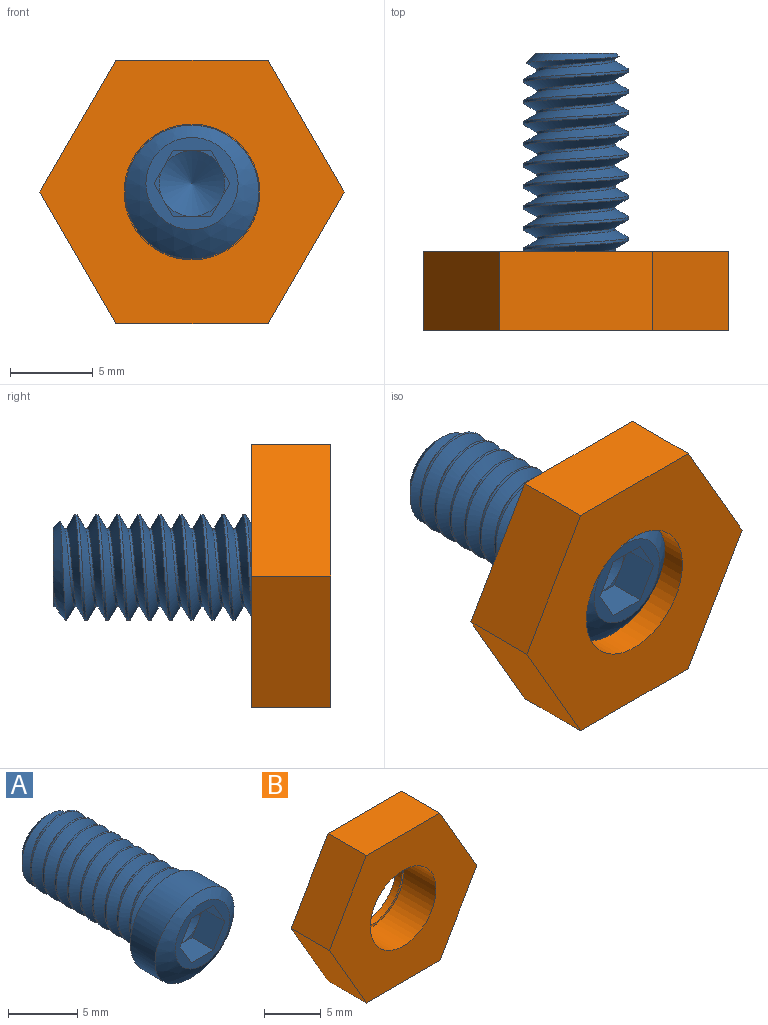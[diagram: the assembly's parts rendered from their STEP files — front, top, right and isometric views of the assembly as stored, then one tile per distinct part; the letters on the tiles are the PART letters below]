
ASSEMBLY  parts=2 mates=1
PART A: 23 faces, bbox 8.1x17.2x8.1 mm
  f0: cylinder r=4.03mm len=8.05mm, axis (0,-1,0), area 63.8mm2, adj f18,f19
  f1: cone r=1.98mm half-angle=60deg, axis (0,-1,0), area 14.2mm2, adj f5,f6,f7,f8,f9,f10
  f2: cylinder r=3.17mm len=11.94mm, axis (0,-1,0), area 29.8mm2, adj f3,f19,f21,f22
  f3: cone r=3.17mm half-angle=45deg, axis (0,-1,0), area 8.5mm2, adj f2,f4,f21,f22
  f4: plane 4.85x4.81mm, normal (0,1,0), area 18.2mm2, adj f3,f20,f21,f22
  f5: plane 1.72x0.99mm, normal (0,-1,0), area 0.2mm2, adj f1,f14,f15
  f6: plane 1.98x0.57mm, normal (0,-1,0), area 0.2mm2, adj f1,f15,f16
  f7: plane 1.72x0.99mm, normal (0,-1,0), area 0.2mm2, adj f1,f11,f16
  f8: plane 1.72x0.99mm, normal (0,-1,0), area 0.2mm2, adj f1,f11,f12
  f9: plane 1.72x0.99mm, normal (0,-1,0), area 0.2mm2, adj f1,f13,f14
  f10: plane 1.98x0.57mm, normal (0,-1,0), area 0.2mm2, adj f1,f12,f13
  f11: plane 2.29x2.21mm, normal (0,0,-1), area 5.1mm2, adj f7,f8,f12,f16,f17
  f12: plane 2.21x1.98mm, normal (-0.87,0,-0.5), area 5.1mm2, adj f8,f10,f11,f13,f17
  f13: plane 2.21x1.98mm, normal (-0.87,0,0.5), area 5.1mm2, adj f9,f10,f12,f14,f17
  f14: plane 2.29x2.21mm, normal (0,0,1), area 5.1mm2, adj f5,f9,f13,f15,f17
  f15: plane 2.21x1.98mm, normal (0.87,0,0.5), area 5.1mm2, adj f5,f6,f14,f16,f17
  f16: plane 2.21x1.98mm, normal (0.87,0,-0.5), area 5.1mm2, adj f6,f7,f11,f15,f17
  f17: plane 5.55x5.55mm, normal (0,-1,0), area 10.6mm2, adj f11,f12,f13,f14,f15,f16,f18
  f18: sphere r=6.42mm, area 32.2mm2, adj f0,f17
  f19: plane 8.05x8.05mm, normal (0,1,0), area 26.7mm2, adj f0,f2,f20,f21,f22
  f20: cylinder r=2.35mm len=12.7mm, axis (0,-1,0), area 23mm2, adj f4,f19,f21,f22
  f21: bspline ~13.65x6.35mm, area 161.6mm2, adj f2,f3,f4,f19,f20
  f22: bspline ~13.34x6.35mm, area 159.7mm2, adj f2,f3,f4,f19,f20
PART B: 11 faces, bbox 18.3x4.8x15.9 mm
  f0: cylinder r=3.87mm len=7.75mm, axis (0,1,0), area 18.5mm2, adj f3,f10
  f1: cylinder r=4.09mm len=8.18mm, axis (0,1,0), area 102.8mm2, adj f2,f3
  f2: plane 18.33x15.88mm, normal (0,-1,0), area 165.7mm2, adj f1,f4,f5,f6,f7,f8,f9
  f3: plane 8.18x8.18mm, normal (0,-1,0), area 5.4mm2, adj f0,f1
  f4: plane 7.94x4.76mm, normal (0.87,0,0.5), area 43.7mm2, adj f2,f5,f9,f10
  f5: plane 9.17x4.76mm, normal (0,0,1), area 43.7mm2, adj f2,f4,f6,f10
  f6: plane 7.94x4.76mm, normal (-0.87,0,0.5), area 43.7mm2, adj f2,f5,f7,f10
  f7: plane 7.94x4.76mm, normal (-0.87,0,-0.5), area 43.7mm2, adj f2,f6,f8,f10
  f8: plane 9.17x4.76mm, normal (0,0,-1), area 43.7mm2, adj f2,f7,f9,f10
  f9: plane 7.94x4.76mm, normal (0.87,0,-0.5), area 43.7mm2, adj f2,f4,f8,f10
  f10: plane 18.33x15.88mm, normal (0,1,0), area 171.1mm2, adj f0,f4,f5,f6,f7,f8,f9
PLACE A t=(4.83,-10.76,10.06)mm fixed
PLACE B t=(4.83,-10.76,10.06)mm
MATE revolute B.f0 <-> A.f0  axis (0,-1,0) through (4.83,-7.41,9.55)mm
